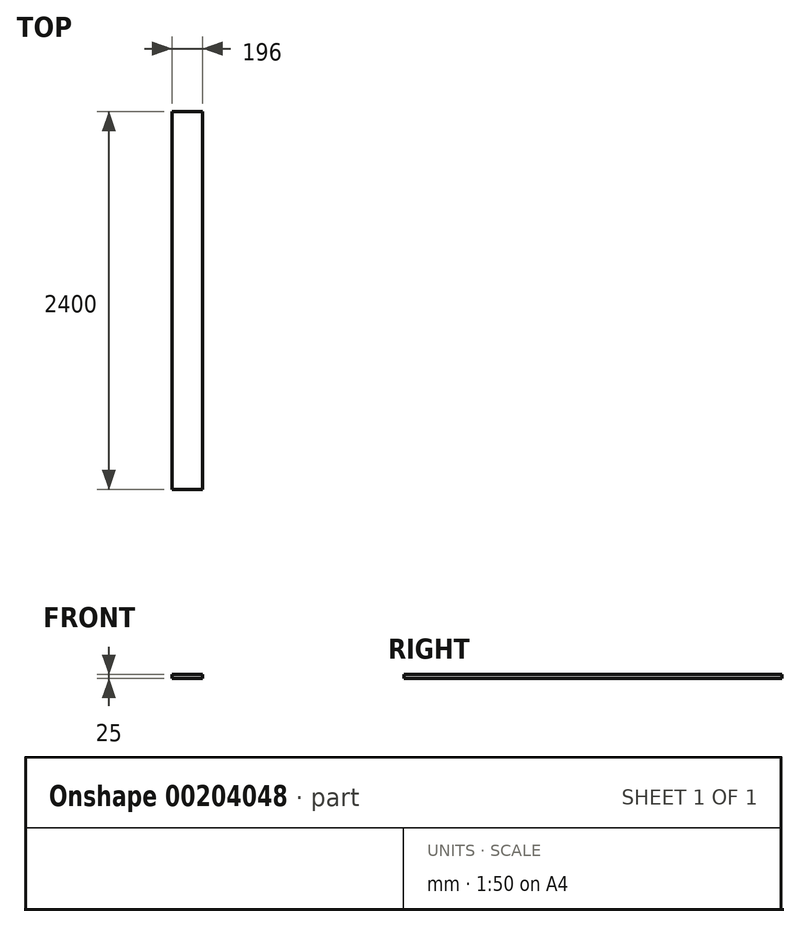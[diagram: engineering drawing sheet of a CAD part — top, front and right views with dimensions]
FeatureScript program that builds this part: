
annotation { "Feature Type Name" : "Feature", "Feature Type Description" : "" }
export const myFeature = defineFeature(function(context is Context, id is Id, definition is map)
    precondition{}
    {
        {
            var Q0;
            Q0=qCreatedBy(makeId("Front.planeOp"),FACE);
            var sketch = newSketch(context, id + "F0", { "sketchPlane" : qUnion([Q0])});
            skLineSegment(sketch, "E0.bottom", {"start": v(0, 0) * mm, "end": v(196, 0) * mm});
            skLineSegment(sketch, "E0.top", {"start": v(0, 25) * mm, "end": v(196, 25) * mm});
            skLineSegment(sketch, "E0.left", {"start": v(0, 0) * mm, "end": v(0, 25) * mm});
            skLineSegment(sketch, "E0.right", {"start": v(196, 0) * mm, "end": v(196, 25) * mm});
            skSolve(sketch);
        }
        {
            var Q0;
            Q0 = qSketchRegion(id + "F0", true);
            extrude(context, id + "F1", {"entities" : qUnion([Q0]), "depth" : 2400 * mm});
        }
    });
